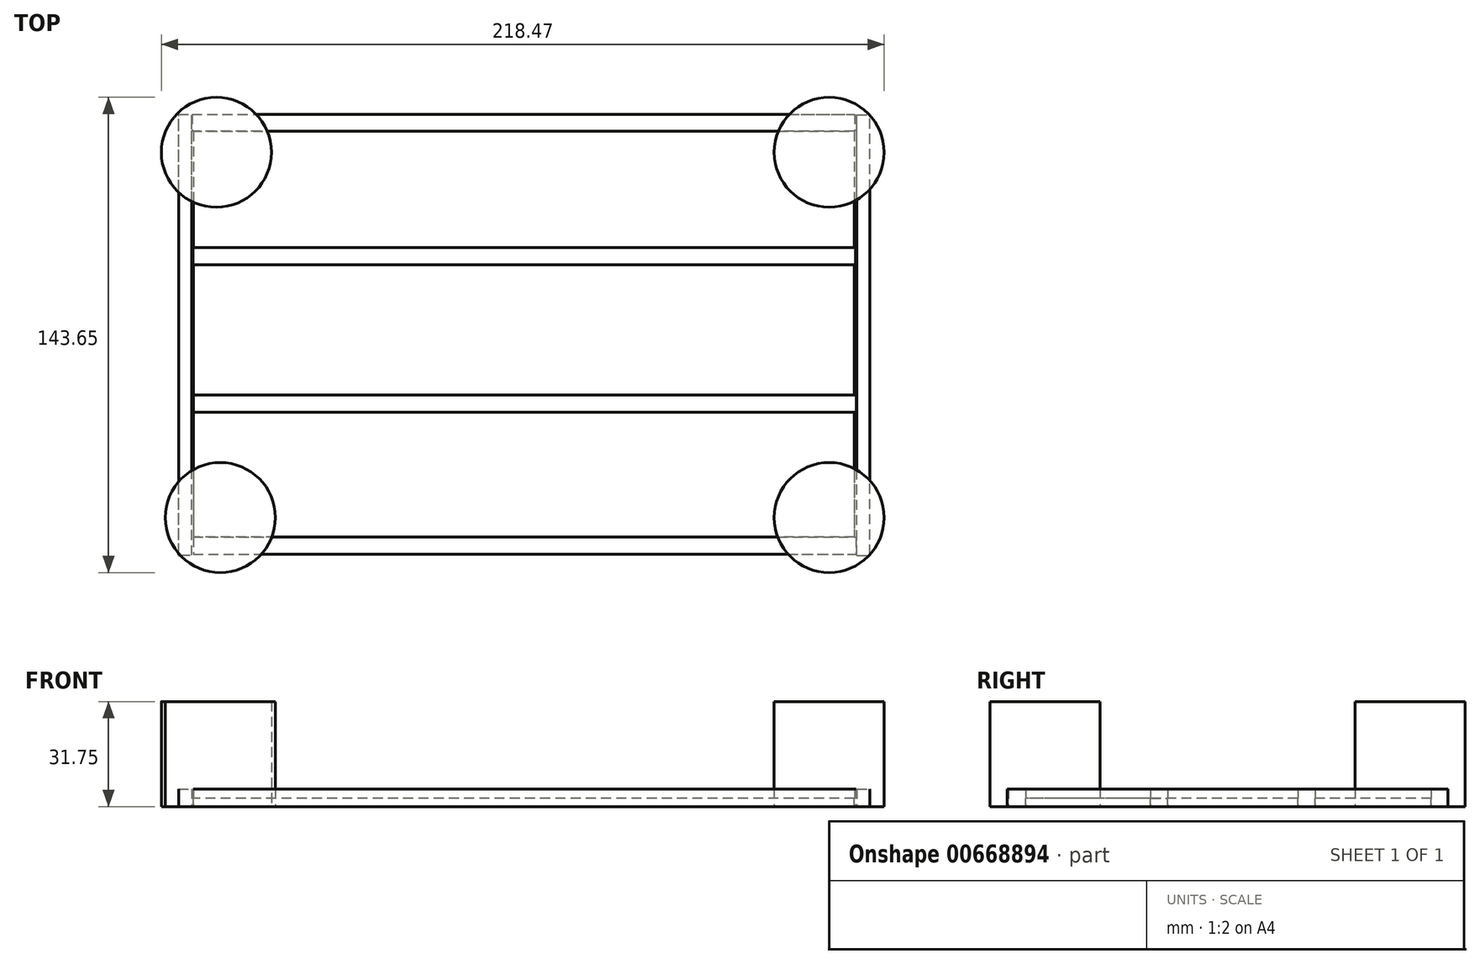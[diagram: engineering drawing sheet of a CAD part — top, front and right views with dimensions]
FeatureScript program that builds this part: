
annotation { "Feature Type Name" : "Feature", "Feature Type Description" : "" }
export const myFeature = defineFeature(function(context is Context, id is Id, definition is map)
    precondition{}
    {
        {
            var Q0;
            Q0=qCreatedBy(makeId("Top.planeOp"),FACE);
            var sketch = newSketch(context, id + "F0", { "sketchPlane" : qUnion([Q0])});
            skLineSegment(sketch, "E0.bottom", {"start": v(-100.34, 76.7) * mm, "end": v(-94.28, 76.7) * mm});
            skLineSegment(sketch, "E0.top", {"start": v(-100.34, -55.92) * mm, "end": v(-94.28, -55.92) * mm});
            skLineSegment(sketch, "E0.left", {"start": v(-100.34, 76.7) * mm, "end": v(-100.34, -55.92) * mm});
            skLineSegment(sketch, "E0.right", {"start": v(-94.28, 76.7) * mm, "end": v(-94.28, -55.92) * mm});
            skLineSegment(sketch, "E1.bottom", {"start": v(-94.28, 76.7) * mm, "end": v(-88.22, 76.7) * mm});
            skLineSegment(sketch, "E1.top", {"start": v(-94.28, -55.92) * mm, "end": v(-88.22, -55.92) * mm});
            skLineSegment(sketch, "E1.right", {"start": v(-88.22, 76.7) * mm, "end": v(-88.22, -55.92) * mm});
            skLineSegment(sketch, "E2.bottom", {"start": v(-88.22, 76.7) * mm, "end": v(-82.17, 76.7) * mm});
            skLineSegment(sketch, "E2.top", {"start": v(-88.22, -55.92) * mm, "end": v(-82.17, -55.92) * mm});
            skLineSegment(sketch, "E2.right", {"start": v(-82.17, 76.7) * mm, "end": v(-82.17, -55.92) * mm});
            skLineSegment(sketch, "E3.bottom", {"start": v(-82.17, 76.7) * mm, "end": v(-76.11, 76.7) * mm});
            skLineSegment(sketch, "E3.top", {"start": v(-82.17, -55.92) * mm, "end": v(-76.11, -55.92) * mm});
            skLineSegment(sketch, "E3.right", {"start": v(-76.11, 76.7) * mm, "end": v(-76.11, -55.92) * mm});
            skLineSegment(sketch, "E4.bottom", {"start": v(-76.11, 76.7) * mm, "end": v(-70.06, 76.7) * mm});
            skLineSegment(sketch, "E4.top", {"start": v(-76.11, -55.92) * mm, "end": v(-70.06, -55.92) * mm});
            skLineSegment(sketch, "E4.right", {"start": v(-70.06, 76.7) * mm, "end": v(-70.06, -55.92) * mm});
            skLineSegment(sketch, "E5.bottom", {"start": v(-70.06, 76.7) * mm, "end": v(-64, 76.7) * mm});
            skLineSegment(sketch, "E5.top", {"start": v(-70.06, -55.92) * mm, "end": v(-64, -55.92) * mm});
            skLineSegment(sketch, "E5.right", {"start": v(-64, 76.7) * mm, "end": v(-64, -55.92) * mm});
            skLineSegment(sketch, "E6.bottom", {"start": v(-64, 76.7) * mm, "end": v(-57.95, 76.7) * mm});
            skLineSegment(sketch, "E6.top", {"start": v(-64, -55.92) * mm, "end": v(-57.95, -55.92) * mm});
            skLineSegment(sketch, "E6.right", {"start": v(-57.95, 76.7) * mm, "end": v(-57.95, -55.92) * mm});
            skLineSegment(sketch, "E7.bottom", {"start": v(-57.95, 76.7) * mm, "end": v(-51.89, 76.7) * mm});
            skLineSegment(sketch, "E7.top", {"start": v(-57.95, -55.92) * mm, "end": v(-51.89, -55.92) * mm});
            skLineSegment(sketch, "E7.right", {"start": v(-51.89, 76.7) * mm, "end": v(-51.89, -55.92) * mm});
            skLineSegment(sketch, "E8.bottom", {"start": v(-51.89, 76.7) * mm, "end": v(-45.83, 76.7) * mm});
            skLineSegment(sketch, "E8.top", {"start": v(-51.89, -55.92) * mm, "end": v(-45.83, -55.92) * mm});
            skLineSegment(sketch, "E8.right", {"start": v(-45.83, 76.7) * mm, "end": v(-45.83, -55.92) * mm});
            skLineSegment(sketch, "E9.bottom", {"start": v(-45.83, 76.7) * mm, "end": v(-39.78, 76.7) * mm});
            skLineSegment(sketch, "E9.top", {"start": v(-45.83, -55.92) * mm, "end": v(-39.78, -55.92) * mm});
            skLineSegment(sketch, "E9.right", {"start": v(-39.78, 76.7) * mm, "end": v(-39.78, -55.92) * mm});
            skLineSegment(sketch, "E10.bottom", {"start": v(-39.78, 76.7) * mm, "end": v(-33.72, 76.7) * mm});
            skLineSegment(sketch, "E10.top", {"start": v(-39.78, -55.92) * mm, "end": v(-33.72, -55.92) * mm});
            skLineSegment(sketch, "E10.right", {"start": v(-33.72, 76.7) * mm, "end": v(-33.72, -55.92) * mm});
            skLineSegment(sketch, "E11.bottom", {"start": v(-33.72, 76.7) * mm, "end": v(-27.67, 76.7) * mm});
            skLineSegment(sketch, "E11.top", {"start": v(-33.72, -55.92) * mm, "end": v(-27.67, -55.92) * mm});
            skLineSegment(sketch, "E11.right", {"start": v(-27.67, 76.7) * mm, "end": v(-27.67, -55.92) * mm});
            skLineSegment(sketch, "E12.bottom", {"start": v(-27.67, 76.7) * mm, "end": v(-21.61, 76.7) * mm});
            skLineSegment(sketch, "E12.top", {"start": v(-27.67, -55.92) * mm, "end": v(-21.61, -55.92) * mm});
            skLineSegment(sketch, "E12.right", {"start": v(-21.61, 76.7) * mm, "end": v(-21.61, -55.92) * mm});
            skLineSegment(sketch, "E13.bottom", {"start": v(-21.61, 76.7) * mm, "end": v(-15.56, 76.7) * mm});
            skLineSegment(sketch, "E13.top", {"start": v(-21.61, -55.92) * mm, "end": v(-15.56, -55.92) * mm});
            skLineSegment(sketch, "E13.right", {"start": v(-15.56, 76.7) * mm, "end": v(-15.56, -55.92) * mm});
            skLineSegment(sketch, "E14.bottom", {"start": v(-15.56, 76.7) * mm, "end": v(-9.5, 76.7) * mm});
            skLineSegment(sketch, "E14.top", {"start": v(-15.56, -55.92) * mm, "end": v(-9.5, -55.92) * mm});
            skLineSegment(sketch, "E14.right", {"start": v(-9.5, 76.7) * mm, "end": v(-9.5, -55.92) * mm});
            skLineSegment(sketch, "E15.bottom", {"start": v(-9.5, 76.7) * mm, "end": v(-3.44, 76.7) * mm});
            skLineSegment(sketch, "E15.top", {"start": v(-9.5, -55.92) * mm, "end": v(-3.44, -55.92) * mm});
            skLineSegment(sketch, "E15.right", {"start": v(-3.44, 76.7) * mm, "end": v(-3.44, -55.92) * mm});
            skLineSegment(sketch, "E16.bottom", {"start": v(-3.44, 76.7) * mm, "end": v(2.61, 76.7) * mm});
            skLineSegment(sketch, "E16.top", {"start": v(-3.44, -55.92) * mm, "end": v(2.61, -55.92) * mm});
            skLineSegment(sketch, "E16.right", {"start": v(2.61, 76.7) * mm, "end": v(2.61, -55.92) * mm});
            skLineSegment(sketch, "E17.bottom", {"start": v(2.61, 76.7) * mm, "end": v(8.67, 76.7) * mm});
            skLineSegment(sketch, "E17.top", {"start": v(2.61, -55.92) * mm, "end": v(8.67, -55.92) * mm});
            skLineSegment(sketch, "E17.right", {"start": v(8.67, 76.7) * mm, "end": v(8.67, -55.92) * mm});
            skLineSegment(sketch, "E18.bottom", {"start": v(8.67, 76.7) * mm, "end": v(14.72, 76.7) * mm});
            skLineSegment(sketch, "E18.top", {"start": v(8.67, -55.92) * mm, "end": v(14.72, -55.92) * mm});
            skLineSegment(sketch, "E18.right", {"start": v(14.72, 76.7) * mm, "end": v(14.72, -55.92) * mm});
            skLineSegment(sketch, "E19.bottom", {"start": v(14.72, 76.7) * mm, "end": v(20.78, 76.7) * mm});
            skLineSegment(sketch, "E19.top", {"start": v(14.72, -55.92) * mm, "end": v(20.78, -55.92) * mm});
            skLineSegment(sketch, "E19.right", {"start": v(20.78, 76.7) * mm, "end": v(20.78, -55.92) * mm});
            skLineSegment(sketch, "E20.bottom", {"start": v(20.78, 76.7) * mm, "end": v(26.83, 76.7) * mm});
            skLineSegment(sketch, "E20.top", {"start": v(20.78, -55.92) * mm, "end": v(26.83, -55.92) * mm});
            skLineSegment(sketch, "E20.right", {"start": v(26.83, 76.7) * mm, "end": v(26.83, -55.92) * mm});
            skLineSegment(sketch, "E21.bottom", {"start": v(26.83, 76.7) * mm, "end": v(32.89, 76.7) * mm});
            skLineSegment(sketch, "E21.top", {"start": v(26.83, -55.92) * mm, "end": v(32.89, -55.92) * mm});
            skLineSegment(sketch, "E21.right", {"start": v(32.89, 76.7) * mm, "end": v(32.89, -55.92) * mm});
            skLineSegment(sketch, "E22.bottom", {"start": v(32.89, 76.7) * mm, "end": v(38.95, 76.7) * mm});
            skLineSegment(sketch, "E22.top", {"start": v(32.89, -55.92) * mm, "end": v(38.95, -55.92) * mm});
            skLineSegment(sketch, "E22.right", {"start": v(38.95, 76.7) * mm, "end": v(38.95, -55.92) * mm});
            skLineSegment(sketch, "E23.bottom", {"start": v(38.95, 76.7) * mm, "end": v(45, 76.7) * mm});
            skLineSegment(sketch, "E23.top", {"start": v(38.95, -55.92) * mm, "end": v(45, -55.92) * mm});
            skLineSegment(sketch, "E23.right", {"start": v(45, 76.7) * mm, "end": v(45, -55.92) * mm});
            skLineSegment(sketch, "E24.bottom", {"start": v(45, 76.7) * mm, "end": v(51.06, 76.7) * mm});
            skLineSegment(sketch, "E24.top", {"start": v(45, -55.92) * mm, "end": v(51.06, -55.92) * mm});
            skLineSegment(sketch, "E24.right", {"start": v(51.06, 76.7) * mm, "end": v(51.06, -55.92) * mm});
            skLineSegment(sketch, "E25.bottom", {"start": v(51.06, 76.7) * mm, "end": v(57.11, 76.7) * mm});
            skLineSegment(sketch, "E25.top", {"start": v(51.06, -55.92) * mm, "end": v(57.11, -55.92) * mm});
            skLineSegment(sketch, "E25.right", {"start": v(57.11, 76.7) * mm, "end": v(57.11, -55.92) * mm});
            skLineSegment(sketch, "E26.bottom", {"start": v(57.11, 76.7) * mm, "end": v(63.17, 76.7) * mm});
            skLineSegment(sketch, "E26.top", {"start": v(57.11, -55.92) * mm, "end": v(63.17, -55.92) * mm});
            skLineSegment(sketch, "E26.right", {"start": v(63.17, 76.7) * mm, "end": v(63.17, -55.92) * mm});
            skLineSegment(sketch, "E27.bottom", {"start": v(63.17, 76.7) * mm, "end": v(69.22, 76.7) * mm});
            skLineSegment(sketch, "E27.top", {"start": v(63.17, -55.92) * mm, "end": v(69.22, -55.92) * mm});
            skLineSegment(sketch, "E27.right", {"start": v(69.22, 76.7) * mm, "end": v(69.22, -55.92) * mm});
            skLineSegment(sketch, "E28.bottom", {"start": v(69.22, 76.7) * mm, "end": v(75.28, 76.7) * mm});
            skLineSegment(sketch, "E28.top", {"start": v(69.22, -55.92) * mm, "end": v(75.28, -55.92) * mm});
            skLineSegment(sketch, "E28.right", {"start": v(75.28, 76.7) * mm, "end": v(75.28, -55.92) * mm});
            skLineSegment(sketch, "E29.bottom", {"start": v(75.28, 76.7) * mm, "end": v(81.34, 76.7) * mm});
            skLineSegment(sketch, "E29.top", {"start": v(75.28, -55.92) * mm, "end": v(81.34, -55.92) * mm});
            skLineSegment(sketch, "E29.right", {"start": v(81.34, 76.7) * mm, "end": v(81.34, -55.92) * mm});
            skLineSegment(sketch, "E30.bottom", {"start": v(81.34, 76.7) * mm, "end": v(87.4, 76.7) * mm});
            skLineSegment(sketch, "E30.top", {"start": v(81.34, -55.92) * mm, "end": v(87.4, -55.92) * mm});
            skLineSegment(sketch, "E30.right", {"start": v(87.4, 76.7) * mm, "end": v(87.4, -55.92) * mm});
            skLineSegment(sketch, "E31.bottom", {"start": v(87.4, 76.7) * mm, "end": v(93.45, 76.7) * mm});
            skLineSegment(sketch, "E31.top", {"start": v(87.4, -55.92) * mm, "end": v(93.45, -55.92) * mm});
            skLineSegment(sketch, "E31.right", {"start": v(93.45, 76.7) * mm, "end": v(93.45, -55.92) * mm});
            skLineSegment(sketch, "E32.bottom", {"start": v(93.45, 76.7) * mm, "end": v(99.5, 76.7) * mm});
            skLineSegment(sketch, "E32.top", {"start": v(93.45, -55.92) * mm, "end": v(99.5, -55.92) * mm});
            skLineSegment(sketch, "E32.right", {"start": v(99.5, 76.7) * mm, "end": v(99.5, -55.92) * mm});
            skSolve(sketch);
        }
        {
            var Q0;
            Q0 = qSketchRegion(id + "F0", true);
            extrude(context, id + "F1", {"entities" : qUnion([Q0]), "depth" : 2.54 * mm, "offsetDistance" : 25.4 * mm});
        }
        {
            var Q0;
            Q0=qCreatedBy(makeId("Top.planeOp"),FACE);
            var sketch = newSketch(context, id + "F2", { "sketchPlane" : qUnion([Q0])});
            skLineSegment(sketch, "E33.bottom", {"start": v(-100.74, 77.02) * mm, "end": v(99.56, 77.02) * mm});
            skLineSegment(sketch, "E33.top", {"start": v(-100.74, 71.85) * mm, "end": v(99.56, 71.85) * mm});
            skLineSegment(sketch, "E33.left", {"start": v(-100.74, 77.02) * mm, "end": v(-100.74, 71.85) * mm});
            skLineSegment(sketch, "E33.right", {"start": v(99.56, 77.02) * mm, "end": v(99.56, 71.85) * mm});
            skLineSegment(sketch, "E34.bottom", {"start": v(-100.43, 36.72) * mm, "end": v(99.87, 36.72) * mm});
            skLineSegment(sketch, "E34.top", {"start": v(-100.43, 31.56) * mm, "end": v(99.87, 31.56) * mm});
            skLineSegment(sketch, "E34.left", {"start": v(-100.43, 36.72) * mm, "end": v(-100.43, 31.56) * mm});
            skLineSegment(sketch, "E34.right", {"start": v(99.87, 36.72) * mm, "end": v(99.87, 31.56) * mm});
            skLineSegment(sketch, "E35.bottom", {"start": v(-100.38, -50.79) * mm, "end": v(99.92, -50.79) * mm});
            skLineSegment(sketch, "E35.top", {"start": v(-100.38, -55.95) * mm, "end": v(99.92, -55.95) * mm});
            skLineSegment(sketch, "E35.left", {"start": v(-100.38, -50.79) * mm, "end": v(-100.38, -55.95) * mm});
            skLineSegment(sketch, "E35.right", {"start": v(99.92, -50.79) * mm, "end": v(99.92, -55.95) * mm});
            skLineSegment(sketch, "E36.bottom", {"start": v(-100.3, -7.85) * mm, "end": v(100.01, -7.85) * mm});
            skLineSegment(sketch, "E36.top", {"start": v(-100.3, -13) * mm, "end": v(100.01, -13) * mm});
            skLineSegment(sketch, "E36.left", {"start": v(-100.3, -7.85) * mm, "end": v(-100.3, -13) * mm});
            skLineSegment(sketch, "E36.right", {"start": v(100.01, -7.85) * mm, "end": v(100.01, -13) * mm});
            skSolve(sketch);
        }
        {
            var Q0;
            Q0=sQuery(id+"F2.wireOp",EDGE,"E33.right");
            var Q1;
            Q1=sQuery(id+"F2.wireOp",EDGE,"E33.bottom");
            var Q2;
            Q2=sQuery(id+"F2.wireOp",EDGE,"E33.top");
            var Q3;
            Q3=sQuery(id+"F2.wireOp",EDGE,"E33.left");
            extrude(context, id + "F3", {"bodyType" : ToolBodyType.SURFACE, "surfaceEntities" : qUnion([Q0, Q1, Q2, Q3]), "depth" : 5.33 * mm, "offsetDistance" : 25.4 * mm});
        }
        {
            var Q0;
            Q0=makeQuery(id+"F2.imprint","IMPRINT",FACE,{"disambiguationData":[TD([[makeQuery(id+"F2.imprint","IMPRINT",EDGE,{"derivedFrom":sQuery(id+"F2.wireOp",EDGE,"E34.bottom")}),-1.0]])]});
            extrude(context, id + "F4", {"entities" : qUnion([Q0]), "operationType" : NewBodyOperationType.ADD, "depth" : 5.33 * mm, "offsetDistance" : 25.4 * mm});
        }
        {
            var Q0;
            Q0=makeQuery(id+"F2.imprint","IMPRINT",FACE,{"disambiguationData":[TD([[makeQuery(id+"F2.imprint","IMPRINT",EDGE,{"derivedFrom":sQuery(id+"F2.wireOp",EDGE,"E36.bottom")}),-1.0]])]});
            extrude(context, id + "F5", {"entities" : qUnion([Q0]), "operationType" : NewBodyOperationType.ADD, "depth" : 5.33 * mm, "offsetDistance" : 25.4 * mm});
        }
        {
            var Q0;
            Q0 = qSketchRegion(id + "F2", true);
            extrude(context, id + "F6", {"entities" : qUnion([Q0]), "operationType" : NewBodyOperationType.ADD, "depth" : 5.33 * mm, "offsetDistance" : 25.4 * mm});
        }
        {
            var Q0;
            Q0=qCreatedBy(makeId("Top.planeOp"),FACE);
            var sketch = newSketch(context, id + "F7", { "sketchPlane" : qUnion([Q0])});
            skLineSegment(sketch, "E37.bottom", {"start": v(100.19, -56.36) * mm, "end": v(104.12, -56.36) * mm});
            skLineSegment(sketch, "E37.top", {"start": v(100.19, 76.85) * mm, "end": v(104.12, 76.85) * mm});
            skLineSegment(sketch, "E37.left", {"start": v(100.19, -56.36) * mm, "end": v(100.19, 76.85) * mm});
            skLineSegment(sketch, "E37.right", {"start": v(104.12, -56.36) * mm, "end": v(104.12, 76.85) * mm});
            skLineSegment(sketch, "E38.bottom", {"start": v(-104.81, -56.28) * mm, "end": v(-100.89, -56.28) * mm});
            skLineSegment(sketch, "E38.top", {"start": v(-104.81, 76.92) * mm, "end": v(-100.89, 76.92) * mm});
            skLineSegment(sketch, "E38.left", {"start": v(-104.81, -56.28) * mm, "end": v(-104.81, 76.92) * mm});
            skLineSegment(sketch, "E38.right", {"start": v(-100.89, -56.28) * mm, "end": v(-100.89, 76.92) * mm});
            skSolve(sketch);
        }
        {
            var Q0;
            Q0 = qSketchRegion(id + "F7", true);
            extrude(context, id + "F8", {"entities" : qUnion([Q0]), "depth" : 5.33 * mm, "offsetDistance" : 25.4 * mm});
        }
        {
            var Q0;
            Q0=qCreatedBy(makeId("Top.planeOp"),FACE);
            var sketch = newSketch(context, id + "F9", { "sketchPlane" : qUnion([Q0])});
            skCircle(sketch, "E39", {"center": v(91.84, 65.51) * mm, "radius": 16.62 * mm});
            skCircle(sketch, "E40", {"center": v(91.84, -44.9) * mm, "radius": 16.62 * mm});
            skCircle(sketch, "E41", {"center": v(-93.4, 65.51) * mm, "radius": 16.62 * mm});
            skCircle(sketch, "E42", {"center": v(-92.2, -44.9) * mm, "radius": 16.62 * mm});
            skSolve(sketch);
        }
        {
            var Q0;
            Q0 = qSketchRegion(id + "F9", true);
            extrude(context, id + "F10", {"entities" : qUnion([Q0]), "depth" : 31.75 * mm, "offsetDistance" : 25.4 * mm});
        }
    });
